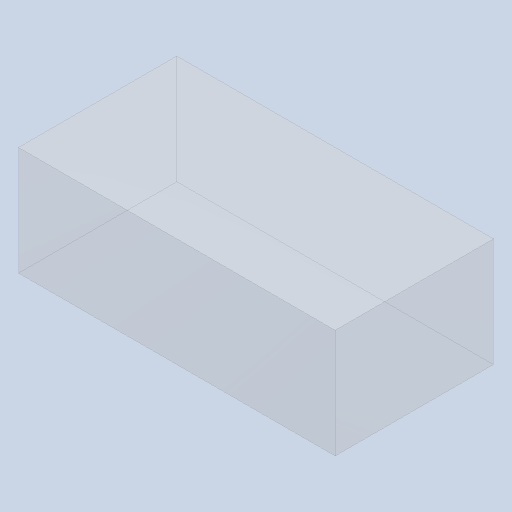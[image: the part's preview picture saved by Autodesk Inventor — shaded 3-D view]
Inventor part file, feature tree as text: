
AUTODESK INVENTOR PART (.ipt)
format: ipt  version: 2022 (Build 260153000, 153)  size: 89,088 bytes
history: imported  units: in
note: dims shown in document units (in); Inventor stores cm internally (conversion verified against a paired STEP export)
features: imported_body x1
ambient origin geometry x8: Origin, YZ Plane, XZ Plane, XY Plane, X Axis, Y Axis, Z Axis, Center Point
bodies: Solid1 (imported_parasolid)
feature tree (1):
  imported_body  NMx_Import_Brep_tag  [imported B-rep: ~6 faces, bbox_mm=[1.6, 0.55, 0.8]]
